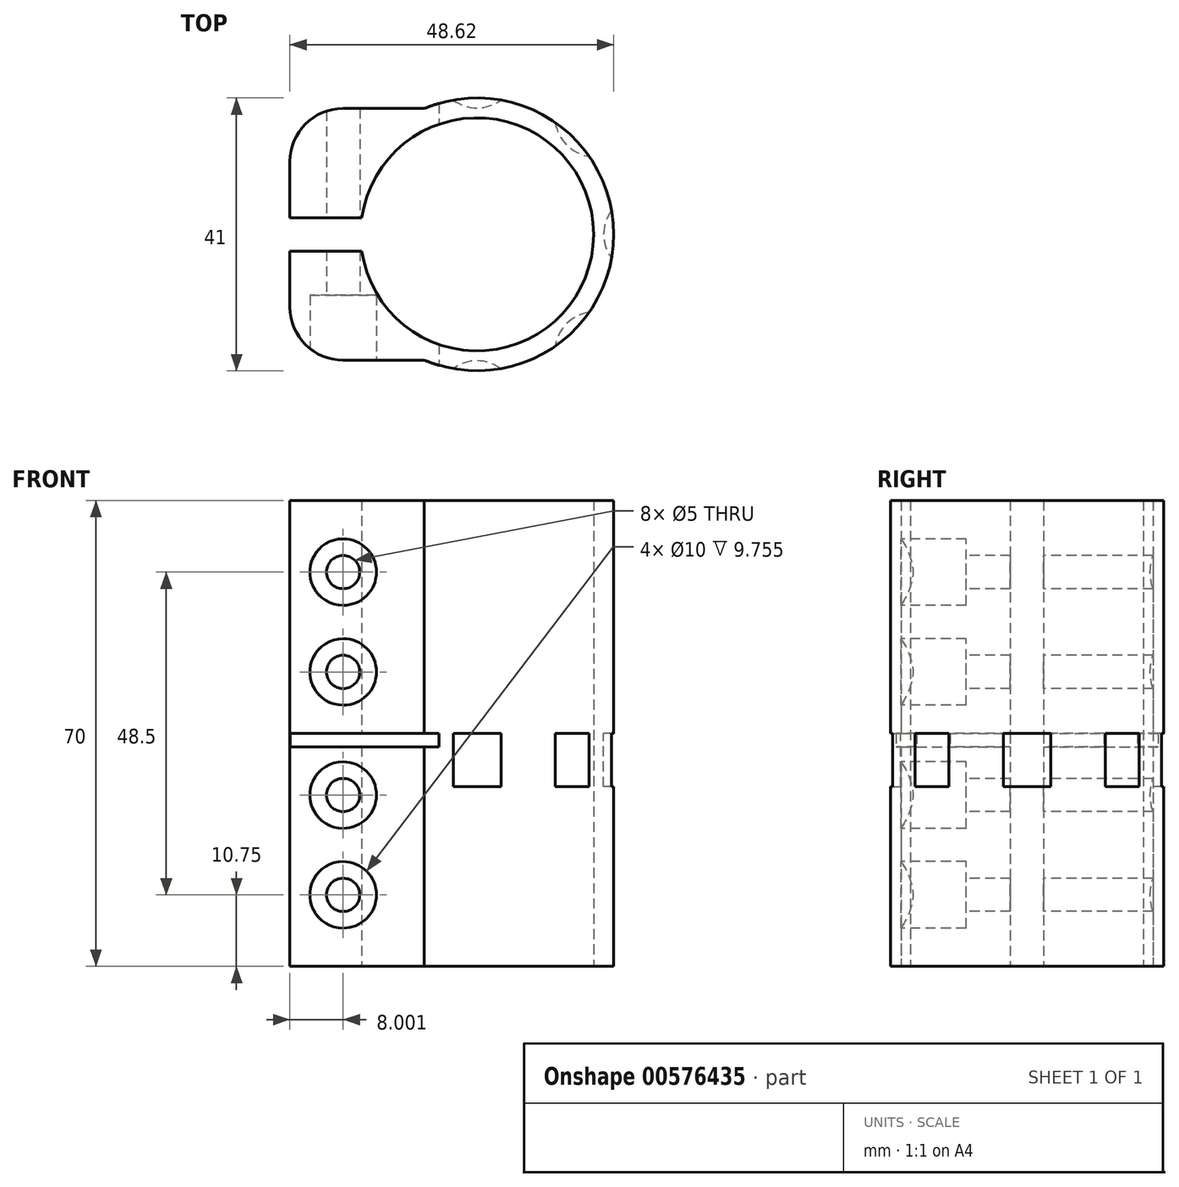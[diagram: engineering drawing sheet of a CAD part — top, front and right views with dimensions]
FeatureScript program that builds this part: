
annotation { "Feature Type Name" : "Feature", "Feature Type Description" : "" }
export const myFeature = defineFeature(function(context is Context, id is Id, definition is map)
    precondition{}
    {
        {
            var Q0;
            Q0=qCreatedBy(makeId("Top.planeOp"),FACE);
            var sketch = newSketch(context, id + "F0", { "sketchPlane" : qUnion([Q0])});
            skArc(sketch, "E0", {"start": v(-17.32, -2.5) * mm, "mid": v(17.5, 0) * mm, "end": v(-17.32, 2.5) * mm});
            skArc(sketch, "E1", {"start": v(-20.35, -2.5) * mm, "mid": v(17.73, -10.29) * mm, "end": v(-7.92, 18.9) * mm});
            skLineSegment(sketch, "E2", {"start": v(-17.32, 2.5) * mm, "end": v(-28.12, 2.5) * mm});
            skLineSegment(sketch, "E3", {"start": v(-28.12, 2.5) * mm, "end": v(-28.12, 10.9) * mm});
            skLineSegment(sketch, "E4", {"start": v(-20.12, 18.9) * mm, "end": v(-7.92, 18.9) * mm});
            skPoint(sketch, "E5.visualSharp", {"position": v(-28.12, 18.9) * mm});
            skArc(sketch, "E5.filletArc", {"start": v(-20.12, 18.9) * mm, "mid": v(-25.78, 16.57) * mm, "end": v(-28.12, 10.9) * mm});
            skLineSegment(sketch, "E6", {"start": v(0, 0) * mm, "end": v(48.86, 0) * mm, "construction": true});
            skLineSegment(sketch, "E7.MirrorCS", {"start": v(-17.32, -2.5) * mm, "end": v(-28.12, -2.5) * mm});
            skLineSegment(sketch, "E8.MirrorCS", {"start": v(-20.12, -18.9) * mm, "end": v(-7.92, -18.9) * mm});
            skLineSegment(sketch, "E9.MirrorCS", {"start": v(-28.12, -2.5) * mm, "end": v(-28.12, -10.9) * mm});
            skArc(sketch, "E10.MirrorCS", {"start": v(-20.12, -18.9) * mm, "mid": v(-25.78, -16.57) * mm, "end": v(-28.12, -10.9) * mm});
            skSolve(sketch);
        }
        {
            var Q0;
            Q0 = qSketchRegion(id + "F0", true);
            extrude(context, id + "F1", {"entities" : qUnion([Q0]), "endBound" : BoundingType.SYMMETRIC, "depth" : 70 * mm, "offsetDistance" : 25 * mm});
        }
        {
            var Q0;
            Q0=makeQuery(id+"F1.opExtrude","SWEPT_FACE",FACE,{"disambiguationData":[OSD([sQuery(id+"F0.wireOp",EDGE,"E8.MirrorCS")])]});
            var sketch = newSketch(context, id + "F2", { "sketchPlane" : qUnion([Q0])});
            skPoint(sketch, "E11", {"position": v(-20.12, -24.25) * mm});
            skPoint(sketch, "E12", {"position": v(-20.12, -9.25) * mm});
            skPoint(sketch, "E13", {"position": v(-20.12, 9.25) * mm});
            skPoint(sketch, "E14", {"position": v(-20.12, 24.25) * mm});
            skSolve(sketch);
        }
        {
            var Q0;
            Q0=sQuery(id+"F2.wireOp",VERTEX,"E11");
            var Q1;
            Q1=sQuery(id+"F2.wireOp",VERTEX,"E12");
            var Q2;
            Q2=sQuery(id+"F2.wireOp",VERTEX,"E13");
            var Q3;
            Q3=sQuery(id+"F2.wireOp",VERTEX,"E14");
            var Q4;
            Q4=makeQuery(id+"F1.opExtrude","SWEPT_BODY",BODY,{"disambiguationData":[OSD([sQuery(id+"F0.wireOp",EDGE,"E0"),sQuery(id+"F0.wireOp",EDGE,"E1"),sQuery(id+"F0.wireOp",EDGE,"E2"),sQuery(id+"F0.wireOp",EDGE,"E3"),sQuery(id+"F0.wireOp",EDGE,"E4"),sQuery(id+"F0.wireOp",EDGE,"E5.filletArc"),sQuery(id+"F0.wireOp",EDGE,"E7.MirrorCS"),sQuery(id+"F0.wireOp",EDGE,"E8.MirrorCS"),sQuery(id+"F0.wireOp",EDGE,"E9.MirrorCS"),sQuery(id+"F0.wireOp",EDGE,"E10.MirrorCS")])]});
            hole(context, id + "F3", {"style" : HoleStyle.C_BORE, "endStyle" : HoleEndStyle.THROUGH, "holeDiameter" : 5 * mm, "cBoreDiameter" : 10 * mm, "cBoreDepth" : 8 * mm, "majorDiameter" : 5 * mm, "isTappedThrough" : true, "tappedDepth" : 12 * mm, "tapClearance" : 3, "locations" : qUnion([Q0, Q1, Q2, Q3]), "scope" : qUnion([Q4])});
        }
        {
            var Q0;
            Q0=qCreatedBy(makeId("Front.planeOp"),FACE);
            var sketch = newSketch(context, id + "F4", { "sketchPlane" : qUnion([Q0])});
            skLineSegment(sketch, "E15.bottom", {"start": v(-28.1, 0) * mm, "end": v(-5.7, 0) * mm});
            skLineSegment(sketch, "E15.top", {"start": v(-28.1, -2) * mm, "end": v(-5.7, -2) * mm});
            skLineSegment(sketch, "E15.left", {"start": v(-28.1, 0) * mm, "end": v(-28.1, -2) * mm});
            skLineSegment(sketch, "E15.right", {"start": v(-5.7, 0) * mm, "end": v(-5.7, -2) * mm});
            skSolve(sketch);
        }
        {
            var Q0;
            Q0 = qSketchRegion(id + "F4", true);
            extrude(context, id + "F5", {"entities" : qUnion([Q0]), "operationType" : NewBodyOperationType.REMOVE, "endBound" : BoundingType.SYMMETRIC, "oppositeDirection" : true, "depth" : 50 * mm, "offsetDistance" : 25 * mm});
        }
        {
            var Q0;
            Q0=qCreatedBy(makeId("Top.planeOp"),FACE);
            var sketch = newSketch(context, id + "F6", { "sketchPlane" : qUnion([Q0])});
            skCircle(sketch, "E16", {"center": v(0, -25) * mm, "radius": 6 * mm});
            skCircle(sketch, "E17.1.0", {"center": v(17.68, -17.68) * mm, "radius": 6 * mm});
            skCircle(sketch, "E17.2.0", {"center": v(25, 0) * mm, "radius": 6 * mm});
            skCircle(sketch, "E17.3.0", {"center": v(17.68, 17.68) * mm, "radius": 6 * mm});
            skCircle(sketch, "E17.4.0", {"center": v(0, 25) * mm, "radius": 6 * mm});
            skPoint(sketch, "E17.center", {"position": v(0, 0) * mm});
            skLineSegment(sketch, "E17.anchor1", {"start": v(0, 0) * mm, "end": v(0, -25) * mm, "construction": true});
            skLineSegment(sketch, "E17.anchor2", {"start": v(0, 0) * mm, "end": v(0, 25) * mm, "construction": true});
            skSolve(sketch);
        }
        {
            var Q0;
            Q0 = qSketchRegion(id + "F6", true);
            extrude(context, id + "F7", {"entities" : qUnion([Q0]), "operationType" : NewBodyOperationType.REMOVE, "oppositeDirection" : true, "depth" : 8 * mm, "offsetDistance" : 25 * mm});
        }
    });
